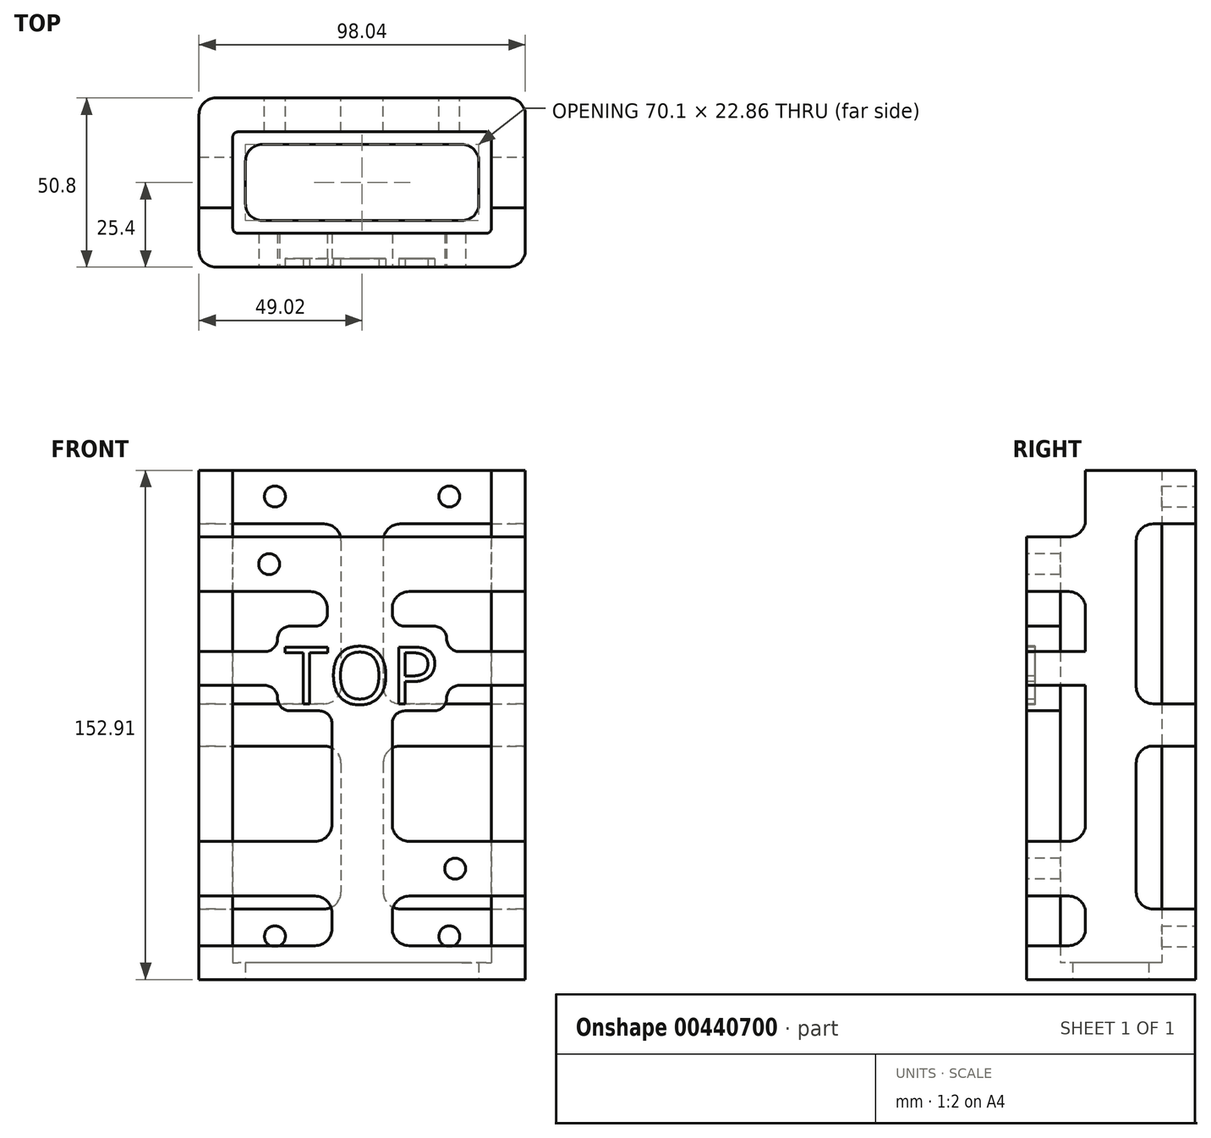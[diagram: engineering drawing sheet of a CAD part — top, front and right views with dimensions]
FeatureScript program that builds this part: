
annotation { "Feature Type Name" : "Feature", "Feature Type Description" : "" }
export const myFeature = defineFeature(function(context is Context, id is Id, definition is map)
    precondition{}
    {
        {
            var Q0;
            Q0=qCreatedBy(makeId("Top.planeOp"),FACE);
            var sketch = newSketch(context, id + "F0", { "sketchPlane" : qUnion([Q0])});
            skLineSegment(sketch, "E0.bottom", {"start": v(38.86, 15.24) * mm, "end": v(-38.86, 15.24) * mm});
            skLineSegment(sketch, "E0.top", {"start": v(38.86, -15.24) * mm, "end": v(-38.86, -15.24) * mm});
            skLineSegment(sketch, "E0.left", {"start": v(38.86, 15.24) * mm, "end": v(38.86, -15.24) * mm});
            skLineSegment(sketch, "E0.right", {"start": v(-38.86, 15.24) * mm, "end": v(-38.86, -15.24) * mm});
            skPoint(sketch, "E0.middle", {"position": v(0, 0) * mm});
            skLineSegment(sketch, "E1.bottom", {"start": v(49.02, -25.4) * mm, "end": v(-49.02, -25.4) * mm});
            skLineSegment(sketch, "E1.top", {"start": v(49.02, 25.4) * mm, "end": v(-49.02, 25.4) * mm});
            skLineSegment(sketch, "E1.left", {"start": v(49.02, -25.4) * mm, "end": v(49.02, 25.4) * mm});
            skLineSegment(sketch, "E1.right", {"start": v(-49.02, -25.4) * mm, "end": v(-49.02, 25.4) * mm});
            skSolve(sketch);
        }
        {
            var Q0;
            Q0 = qSketchRegion(id + "F0", true);
            extrude(context, id + "F1", {"entities" : qUnion([Q0]), "depth" : 152.9 * mm});
        }
        {
            var Q0;
            Q0=makeQuery(id+"F1.opExtrude","SWEPT_FACE",FACE,{"disambiguationData":[OSD([sQuery(id+"F0.wireOp",EDGE,"E1.bottom")])]});
            var sketch = newSketch(context, id + "F2", { "sketchPlane" : qUnion([Q0])});
            skCircle(sketch, "E2", {"center": v(-27.94, 124.71) * mm, "radius": 3.15 * mm});
            skCircle(sketch, "E3", {"center": v(27.94, 33.27) * mm, "radius": 3.15 * mm});
            skLineSegment(sketch, "E4", {"start": v(0, 0) * mm, "end": v(0, 152.9) * mm, "construction": true});
            skSolve(sketch);
        }
        {
            var Q0;
            Q0 = qSketchRegion(id + "F2", true);
            var Q1;
            Q1=makeQuery(id+"F1.opExtrude","SWEPT_FACE",FACE,{"disambiguationData":[OSD([sQuery(id+"F0.wireOp",EDGE,"E0.top")])]});
            extrude(context, id + "F3", {"entities" : qUnion([Q0]), "operationType" : NewBodyOperationType.REMOVE, "endBound" : BoundingType.UP_TO_SURFACE, "oppositeDirection" : true, "endBoundEntityFace" : qUnion([Q1]), "depth" : 25.4 * mm});
        }
        {
            var Q0;
            Q0=makeQuery(id+"F1.opExtrude","SWEPT_FACE",FACE,{"disambiguationData":[OSD([sQuery(id+"F0.wireOp",EDGE,"E1.bottom")])]});
            var sketch = newSketch(context, id + "F4", { "sketchPlane" : qUnion([Q0])});
            skText(sketch, "E5", { "text": "TOP", "fontName": "OpenSans-Regular.ttf"});
            skLineSegment(sketch, "E6", {"start": v(0, 152.9) * mm, "end": v(0, 0) * mm, "construction": true});
            const initialGuessF4  = {"E5": [-0.02337, 0.0827, 1, 0, 0.01728]};
            skSetInitialGuess(sketch, initialGuessF4);
            skSolve(sketch);
        }
        {
            var Q0;
            Q0 = qSketchRegion(id + "F4", true);
            extrude(context, id + "F5", {"entities" : qUnion([Q0]), "operationType" : NewBodyOperationType.REMOVE, "oppositeDirection" : true, "depth" : 2.54 * mm});
        }
        {
            var Q0;
            Q0=makeQuery(id+"F1.opExtrude","SWEPT_FACE",FACE,{"disambiguationData":[OSD([sQuery(id+"F0.wireOp",EDGE,"E1.top")])]});
            var sketch = newSketch(context, id + "F6", { "sketchPlane" : qUnion([Q0])});
            skCircle(sketch, "E7", {"center": v(26.2, 145.03) * mm, "radius": 3.15 * mm});
            skLineSegment(sketch, "E8", {"start": v(0, 0) * mm, "end": v(0, 152.9) * mm, "construction": true});
            skCircle(sketch, "E9.0.1.0", {"center": v(26.2, 12.95) * mm, "radius": 3.15 * mm});
            skCircle(sketch, "E9.1.0.0", {"center": v(-26.2, 145.03) * mm, "radius": 3.15 * mm});
            skCircle(sketch, "E9.1.1.0", {"center": v(-26.2, 12.95) * mm, "radius": 3.15 * mm});
            skLineSegment(sketch, "E9.direction1", {"start": v(26.2, 145.03) * mm, "end": v(-26.2, 145.03) * mm, "construction": true});
            skLineSegment(sketch, "E9.direction2", {"start": v(26.2, 145.03) * mm, "end": v(26.2, 12.95) * mm, "construction": true});
            skSolve(sketch);
        }
        {
            var Q0;
            Q0 = qSketchRegion(id + "F6", true);
            var Q1;
            Q1=makeQuery(id+"F1.opExtrude","SWEPT_FACE",FACE,{"disambiguationData":[OSD([sQuery(id+"F0.wireOp",EDGE,"E0.bottom")])]});
            extrude(context, id + "F7", {"entities" : qUnion([Q0]), "operationType" : NewBodyOperationType.REMOVE, "endBound" : BoundingType.UP_TO_SURFACE, "oppositeDirection" : true, "endBoundEntityFace" : qUnion([Q1]), "depth" : 25.4 * mm});
        }
        {
            var Q0;
            Q0=makeQuery(id+"F1.opExtrude","CAP_FACE",FACE,{"disambiguationData":[OSD([sQuery(id+"F0.wireOp",EDGE,"E0.bottom"),sQuery(id+"F0.wireOp",EDGE,"E0.top"),sQuery(id+"F0.wireOp",EDGE,"E0.left"),sQuery(id+"F0.wireOp",EDGE,"E0.right"),sQuery(id+"F0.wireOp",EDGE,"E1.bottom"),sQuery(id+"F0.wireOp",EDGE,"E1.top"),sQuery(id+"F0.wireOp",EDGE,"E1.left"),sQuery(id+"F0.wireOp",EDGE,"E1.right")])],"isStart":true});
            var sketch = newSketch(context, id + "F8", { "sketchPlane" : qUnion([Q0])});
            skLineSegment(sketch, "E10.bottom", {"start": v(38.86, 15.24) * mm, "end": v(-38.86, 15.24) * mm});
            skLineSegment(sketch, "E10.top", {"start": v(38.86, -15.24) * mm, "end": v(-38.86, -15.24) * mm});
            skLineSegment(sketch, "E10.left", {"start": v(38.86, 15.24) * mm, "end": v(38.86, -15.24) * mm});
            skLineSegment(sketch, "E10.right", {"start": v(-38.86, 15.24) * mm, "end": v(-38.86, -15.24) * mm});
            skPoint(sketch, "E10.middle", {"position": v(0, 0) * mm});
            skLineSegment(sketch, "E11.bottom", {"start": v(35.05, -11.43) * mm, "end": v(-35.05, -11.43) * mm});
            skLineSegment(sketch, "E11.top", {"start": v(35.05, 11.43) * mm, "end": v(-35.05, 11.43) * mm});
            skLineSegment(sketch, "E11.left", {"start": v(35.05, -11.43) * mm, "end": v(35.05, 11.43) * mm});
            skLineSegment(sketch, "E11.right", {"start": v(-35.05, -11.43) * mm, "end": v(-35.05, 11.43) * mm});
            skSolve(sketch);
        }
        {
            var Q0;
            Q0 = qSketchRegion(id + "F8", true);
            extrude(context, id + "F9", {"entities" : qUnion([Q0]), "operationType" : NewBodyOperationType.ADD, "oppositeDirection" : true, "depth" : 5.08 * mm});
        }
        {
            var Q0;
            Q0=makeQuery(id+"F1.opExtrude","SWEPT_EDGE",EDGE,{"disambiguationData":[OSD([sQuery(id+"F0.wireOp",EDGE,"E0.bottom"),sQuery(id+"F0.wireOp",EDGE,"E0.right")])]});
            var Q1;
            Q1=makeQuery(id+"F1.opExtrude","SWEPT_EDGE",EDGE,{"disambiguationData":[OSD([sQuery(id+"F0.wireOp",EDGE,"E0.top"),sQuery(id+"F0.wireOp",EDGE,"E0.right")])]});
            var Q2;
            Q2=makeQuery(id+"F1.opExtrude","SWEPT_EDGE",EDGE,{"disambiguationData":[OSD([sQuery(id+"F0.wireOp",EDGE,"E0.top"),sQuery(id+"F0.wireOp",EDGE,"E0.left")])]});
            var Q3;
            Q3=makeQuery(id+"F1.opExtrude","SWEPT_EDGE",EDGE,{"disambiguationData":[OSD([sQuery(id+"F0.wireOp",EDGE,"E0.bottom"),sQuery(id+"F0.wireOp",EDGE,"E0.left")])]});
            fillet(context, id + "F10", {"entities" : qUnion([Q0, Q1, Q2, Q3]), "radius" : 1.59 * mm, "tangentPropagation" : true, "allowEdgeOverflow" : false});
        }
        {
            var Q0;
            {var subQ1=sQuery(id+"F0.wireOp",EDGE,"E1.left");var subQ3=sQuery(id+"F0.wireOp",EDGE,"E1.bottom");Q0=makeQuery(id+"F5.boolean.opBoolean","SPLIT",FACE,{"disambiguationData":[TD([makeQuery(id+"F1.opExtrude","SWEPT_FACE",FACE,{"disambiguationData":[OSD([subQ1])]})])],"derivedFrom":makeQuery(id+"F1.opExtrude","SWEPT_FACE",FACE,{"disambiguationData":[OSD([subQ3])]})});}
            var sketch = newSketch(context, id + "F11", { "sketchPlane" : qUnion([Q0])});
            skLineSegment(sketch, "E12.bottom", {"start": v(49.02, 25.04) * mm, "end": v(9.05, 25.04) * mm});
            skLineSegment(sketch, "E12.top", {"start": v(49.02, 41.5) * mm, "end": v(9.05, 41.5) * mm});
            skLineSegment(sketch, "E13.left", {"start": v(9.05, 25.04) * mm, "end": v(9.05, 10.16) * mm});
            skLineSegment(sketch, "E13.right", {"start": v(-9.05, 25.04) * mm, "end": v(-9.05, 10.16) * mm});
            skLineSegment(sketch, "E14.trimOffspring", {"start": v(-9.05, 25.04) * mm, "end": v(-49.02, 25.04) * mm});
            skLineSegment(sketch, "E15", {"start": v(0, 0) * mm, "end": v(0, 152.9) * mm, "construction": true});
            skLineSegment(sketch, "E16.bottom", {"start": v(-49.02, 116.48) * mm, "end": v(-10.43, 116.48) * mm});
            skLineSegment(sketch, "E16.top", {"start": v(-49.02, 132.94) * mm, "end": v(9.05, 132.94) * mm});
            skLineSegment(sketch, "E17", {"start": v(49.02, 25.04) * mm, "end": v(49.02, 10.16) * mm});
            skLineSegment(sketch, "E18", {"start": v(49.02, 10.16) * mm, "end": v(9.05, 10.16) * mm});
            skLineSegment(sketch, "E19", {"start": v(-9.05, 10.16) * mm, "end": v(-49.02, 10.16) * mm});
            skLineSegment(sketch, "E20", {"start": v(-49.02, 10.16) * mm, "end": v(-49.02, 25.04) * mm});
            skLineSegment(sketch, "E21.left", {"start": v(9.05, 41.5) * mm, "end": v(9.05, 76.86) * mm});
            skLineSegment(sketch, "E21.right", {"start": v(-9.05, 41.5) * mm, "end": v(-9.05, 76.86) * mm});
            skLineSegment(sketch, "E22", {"start": v(49.02, 41.5) * mm, "end": v(49.02, 41.5) * mm});
            skLineSegment(sketch, "E23", {"start": v(9.05, 109.9) * mm, "end": v(9.05, 116.48) * mm});
            skLineSegment(sketch, "E24", {"start": v(-10.43, 109.9) * mm, "end": v(-10.43, 116.48) * mm});
            skLineSegment(sketch, "E25.trimOffspring", {"start": v(-9.05, 41.5) * mm, "end": v(-49.02, 41.5) * mm});
            skLineSegment(sketch, "E26.trimOffspring", {"start": v(9.05, 116.48) * mm, "end": v(49.02, 116.48) * mm});
            skLineSegment(sketch, "E27", {"start": v(-49.02, 98.46) * mm, "end": v(-49.02, 116.48) * mm});
            skLineSegment(sketch, "E28", {"start": v(49.02, 132.94) * mm, "end": v(49.02, 152.9) * mm});
            skLineSegment(sketch, "E29", {"start": v(49.02, 152.9) * mm, "end": v(-49.02, 152.9) * mm});
            skLineSegment(sketch, "E30", {"start": v(-49.02, 152.9) * mm, "end": v(-49.02, 132.94) * mm});
            skLineSegment(sketch, "E31.right", {"start": v(-49.02, 152.9) * mm, "end": v(-49.02, 152.9) * mm});
            skLineSegment(sketch, "E32.trimOffspring", {"start": v(9.05, 132.94) * mm, "end": v(49.02, 132.94) * mm});
            skLineSegment(sketch, "E33", {"start": v(9.05, 132.94) * mm, "end": v(9.05, 132.94) * mm});
            skPoint(sketch, "E34.visualSharp", {"position": v(-28.45, 89.67) * mm});
            skLineSegment(sketch, "E35", {"start": v(49.02, 116.48) * mm, "end": v(49.02, 98.48) * mm});
            skLineSegment(sketch, "E36", {"start": v(-49.02, 93.38) * mm, "end": v(49.02, 93.38) * mm, "construction": true});
            skLineSegment(sketch, "E37.bottom", {"start": v(-12.86, 80.67) * mm, "end": v(-21.59, 80.67) * mm});
            skLineSegment(sketch, "E37.top", {"start": v(21.59, 106.1) * mm, "end": v(12.86, 106.1) * mm});
            skLineSegment(sketch, "E37.left", {"start": v(25.4, 84.48) * mm, "end": v(25.4, 84.5) * mm});
            skLineSegment(sketch, "E37.right", {"start": v(-25.4, 84.48) * mm, "end": v(-25.4, 84.5) * mm});
            skPoint(sketch, "E37.middle", {"position": v(0, 93.38) * mm});
            skLineSegment(sketch, "E38.bottom", {"start": v(-49.02, 98.46) * mm, "end": v(-29.21, 98.46) * mm});
            skLineSegment(sketch, "E38.top", {"start": v(-49.02, 88.3) * mm, "end": v(-29.21, 88.3) * mm});
            skLineSegment(sketch, "E39.bottom", {"start": v(29.2, 98.48) * mm, "end": v(49.02, 98.48) * mm});
            skLineSegment(sketch, "E39.top", {"start": v(29.21, 88.3) * mm, "end": v(49.02, 88.3) * mm});
            skLineSegment(sketch, "E40.trimOffspring", {"start": v(-25.4, 102.27) * mm, "end": v(-25.4, 102.29) * mm});
            skLineSegment(sketch, "E41.trimOffspring", {"start": v(25.4, 102.29) * mm, "end": v(25.4, 102.29) * mm});
            skPoint(sketch, "E42.visualSharp", {"position": v(25.4, 106.1) * mm});
            skArc(sketch, "E42.filletArc", {"start": v(25.4, 102.29) * mm, "mid": v(24.28, 104.98) * mm, "end": v(21.59, 106.1) * mm});
            skPoint(sketch, "E43.visualSharp", {"position": v(25.4, 98.48) * mm});
            skArc(sketch, "E43.filletArc", {"start": v(25.4, 102.29) * mm, "mid": v(26.52, 99.6) * mm, "end": v(29.2, 98.48) * mm});
            skPoint(sketch, "E44.visualSharp", {"position": v(25.4, 88.3) * mm});
            skArc(sketch, "E44.filletArc", {"start": v(29.21, 88.3) * mm, "mid": v(26.52, 87.19) * mm, "end": v(25.4, 84.5) * mm});
            skPoint(sketch, "E45.visualSharp", {"position": v(25.4, 80.67) * mm});
            skArc(sketch, "E45.filletArc", {"start": v(21.59, 80.67) * mm, "mid": v(24.28, 81.79) * mm, "end": v(25.4, 84.48) * mm});
            skPoint(sketch, "E46.visualSharp", {"position": v(-25.4, 98.46) * mm});
            skArc(sketch, "E46.filletArc", {"start": v(-29.21, 98.46) * mm, "mid": v(-26.52, 99.58) * mm, "end": v(-25.4, 102.27) * mm});
            skPoint(sketch, "E47.visualSharp", {"position": v(-25.4, 106.1) * mm});
            skArc(sketch, "E47.filletArc", {"start": v(-21.6, 106.1) * mm, "mid": v(-24.28, 104.98) * mm, "end": v(-25.4, 102.29) * mm});
            skPoint(sketch, "E48.visualSharp", {"position": v(-25.4, 88.3) * mm});
            skArc(sketch, "E48.filletArc", {"start": v(-25.4, 84.5) * mm, "mid": v(-26.52, 87.19) * mm, "end": v(-29.21, 88.3) * mm});
            skPoint(sketch, "E49.visualSharp", {"position": v(-25.4, 80.67) * mm});
            skArc(sketch, "E49.filletArc", {"start": v(-25.4, 84.48) * mm, "mid": v(-24.28, 81.79) * mm, "end": v(-21.59, 80.67) * mm});
            skPoint(sketch, "E50.newPointA", {"position": v(-9.05, 80.67) * mm});
            skArc(sketch, "E50.filletArc", {"start": v(-9.05, 76.86) * mm, "mid": v(-10.16, 79.55) * mm, "end": v(-12.86, 80.67) * mm});
            skLineSegment(sketch, "E51", {"start": v(12.86, 80.67) * mm, "end": v(21.59, 80.67) * mm});
            skLineSegment(sketch, "E52.trimOffspring", {"start": v(-14.24, 106.1) * mm, "end": v(-21.6, 106.1) * mm});
            skPoint(sketch, "E53.visualSharp", {"position": v(9.05, 80.67) * mm});
            skArc(sketch, "E53.filletArc", {"start": v(12.86, 80.67) * mm, "mid": v(10.16, 79.55) * mm, "end": v(9.05, 76.86) * mm});
            skPoint(sketch, "E54.visualSharp", {"position": v(-10.43, 106.1) * mm});
            skArc(sketch, "E54.filletArc", {"start": v(-14.24, 106.1) * mm, "mid": v(-11.54, 107.21) * mm, "end": v(-10.43, 109.9) * mm});
            skPoint(sketch, "E55.visualSharp", {"position": v(9.05, 106.1) * mm});
            skArc(sketch, "E55.filletArc", {"start": v(9.05, 109.9) * mm, "mid": v(10.16, 107.21) * mm, "end": v(12.86, 106.1) * mm});
            skLineSegment(sketch, "E56", {"start": v(-49.02, 88.3) * mm, "end": v(-49.02, 41.5) * mm});
            skLineSegment(sketch, "E57", {"start": v(49.02, 88.3) * mm, "end": v(49.02, 41.5) * mm});
            skSolve(sketch);
        }
        {
            var Q0;
            Q0 = qSketchRegion(id + "F11", true);
            extrude(context, id + "F12", {"entities" : qUnion([Q0]), "operationType" : NewBodyOperationType.REMOVE, "oppositeDirection" : true, "depth" : 17.78 * mm});
        }
        {
            var Q0;
            Q0=makeQuery(id+"F1.opExtrude","SWEPT_FACE",FACE,{"disambiguationData":[OSD([sQuery(id+"F0.wireOp",EDGE,"E1.top")])]});
            var sketch = newSketch(context, id + "F13", { "sketchPlane" : qUnion([Q0])});
            skLineSegment(sketch, "E58.top", {"start": v(49.02, 21.18) * mm, "end": v(6.35, 21.18) * mm});
            skLineSegment(sketch, "E59.top", {"start": v(49.02, 136.8) * mm, "end": v(6.35, 136.8) * mm});
            skLineSegment(sketch, "E60", {"start": v(49.02, 76.45) * mm, "end": v(-49.02, 76.45) * mm, "construction": true});
            skLineSegment(sketch, "E61.bottom", {"start": v(49.02, 70.1) * mm, "end": v(6.35, 70.1) * mm});
            skLineSegment(sketch, "E61.top", {"start": v(49.02, 82.8) * mm, "end": v(6.35, 82.8) * mm});
            skLineSegment(sketch, "E62", {"start": v(0, 0) * mm, "end": v(0, 152.9) * mm, "construction": true});
            skLineSegment(sketch, "E63.left", {"start": v(6.35, 21.18) * mm, "end": v(6.35, 70.1) * mm});
            skLineSegment(sketch, "E63.right", {"start": v(-6.35, 21.18) * mm, "end": v(-6.35, 70.1) * mm});
            skLineSegment(sketch, "E64.trimOffspring", {"start": v(-6.35, 70.1) * mm, "end": v(-49.02, 70.1) * mm});
            skLineSegment(sketch, "E65.trimOffspring", {"start": v(-6.35, 82.8) * mm, "end": v(-49.02, 82.8) * mm});
            skLineSegment(sketch, "E66.trimOffspring", {"start": v(6.35, 82.8) * mm, "end": v(6.35, 136.8) * mm});
            skLineSegment(sketch, "E67.trimOffspring", {"start": v(-6.35, 82.8) * mm, "end": v(-6.35, 136.8) * mm});
            skLineSegment(sketch, "E68.trimOffspring", {"start": v(-6.35, 21.18) * mm, "end": v(-49.02, 21.18) * mm});
            skLineSegment(sketch, "E69.trimOffspring", {"start": v(-6.35, 136.8) * mm, "end": v(-49.02, 136.8) * mm});
            skLineSegment(sketch, "E70", {"start": v(49.02, 70.1) * mm, "end": v(49.02, 21.18) * mm});
            skLineSegment(sketch, "E71", {"start": v(49.02, 136.8) * mm, "end": v(49.02, 82.8) * mm});
            skLineSegment(sketch, "E72", {"start": v(-49.02, 136.8) * mm, "end": v(-49.02, 82.8) * mm});
            skLineSegment(sketch, "E73", {"start": v(-49.02, 70.1) * mm, "end": v(-49.02, 21.18) * mm});
            skSolve(sketch);
        }
        {
            var Q0;
            Q0 = qSketchRegion(id + "F13", true);
            extrude(context, id + "F14", {"entities" : qUnion([Q0]), "operationType" : NewBodyOperationType.REMOVE, "oppositeDirection" : true, "depth" : 17.78 * mm});
        }
        {
            var Q0;
            Q0=makeQuery(id+"F12.boolean.opBoolean","COPY",EDGE,{"derivedFrom":makeQuery(id+"F12.opExtrude","CAP_EDGE",EDGE,{"disambiguationData":[OSD([sQuery(id+"F11.wireOp",EDGE,"E18")])],"isStart":false})});
            var Q1;
            Q1=makeQuery(id+"F12.boolean.opBoolean","COPY",EDGE,{"derivedFrom":makeQuery(id+"F12.opExtrude","SWEPT_EDGE",EDGE,{"disambiguationData":[OSD([sQuery(id+"F11.wireOp",EDGE,"E13.left"),sQuery(id+"F11.wireOp",EDGE,"E18")])]})});
            var Q2;
            Q2=makeQuery(id+"F12.boolean.opBoolean","COPY",EDGE,{"derivedFrom":makeQuery(id+"F12.opExtrude","SWEPT_EDGE",EDGE,{"disambiguationData":[OSD([sQuery(id+"F11.wireOp",EDGE,"E12.bottom"),sQuery(id+"F11.wireOp",EDGE,"E13.left")])]})});
            var Q3;
            Q3=makeQuery(id+"F12.boolean.opBoolean","COPY",EDGE,{"derivedFrom":makeQuery(id+"F12.opExtrude","CAP_EDGE",EDGE,{"disambiguationData":[OSD([sQuery(id+"F11.wireOp",EDGE,"E12.bottom")])],"isStart":false})});
            var Q4;
            Q4=makeQuery(id+"F12.boolean.opBoolean","COPY",EDGE,{"derivedFrom":makeQuery(id+"F12.opExtrude","SWEPT_EDGE",EDGE,{"disambiguationData":[OSD([sQuery(id+"F11.wireOp",EDGE,"E13.right"),sQuery(id+"F11.wireOp",EDGE,"E19")])]})});
            var Q5;
            Q5=makeQuery(id+"F12.boolean.opBoolean","COPY",EDGE,{"derivedFrom":makeQuery(id+"F12.opExtrude","SWEPT_EDGE",EDGE,{"disambiguationData":[OSD([sQuery(id+"F11.wireOp",EDGE,"E13.right"),sQuery(id+"F11.wireOp",EDGE,"E14.trimOffspring")])]})});
            var Q6;
            Q6=makeQuery(id+"F12.boolean.opBoolean","COPY",EDGE,{"derivedFrom":makeQuery(id+"F12.opExtrude","CAP_EDGE",EDGE,{"disambiguationData":[OSD([sQuery(id+"F11.wireOp",EDGE,"E14.trimOffspring")])],"isStart":false})});
            var Q7;
            Q7=makeQuery(id+"F12.boolean.opBoolean","COPY",EDGE,{"derivedFrom":makeQuery(id+"F12.opExtrude","CAP_EDGE",EDGE,{"disambiguationData":[OSD([sQuery(id+"F11.wireOp",EDGE,"E19")])],"isStart":false})});
            var Q8;
            Q8=makeQuery(id+"F12.boolean.opBoolean","COPY",EDGE,{"derivedFrom":makeQuery(id+"F12.opExtrude","CAP_EDGE",EDGE,{"disambiguationData":[OSD([sQuery(id+"F11.wireOp",EDGE,"E25.trimOffspring")])],"isStart":false})});
            var Q9;
            Q9=makeQuery(id+"F12.boolean.opBoolean","COPY",EDGE,{"derivedFrom":makeQuery(id+"F12.opExtrude","SWEPT_EDGE",EDGE,{"disambiguationData":[OSD([sQuery(id+"F11.wireOp",EDGE,"E21.right"),sQuery(id+"F11.wireOp",EDGE,"E25.trimOffspring")])]})});
            var Q10;
            Q10=makeQuery(id+"F12.boolean.opBoolean","COPY",EDGE,{"derivedFrom":makeQuery(id+"F12.opExtrude","SWEPT_EDGE",EDGE,{"disambiguationData":[OSD([sQuery(id+"F11.wireOp",EDGE,"E21.right"),sQuery(id+"F11.wireOp",EDGE,"4d2d0d0c-2c55-4c6a-b625-4996a5f88d60.trimOffspring")])]})});
            var Q11;
            Q11=makeQuery(id+"F12.boolean.opBoolean","COPY",EDGE,{"derivedFrom":makeQuery(id+"F12.opExtrude","CAP_EDGE",EDGE,{"disambiguationData":[OSD([sQuery(id+"F11.wireOp",EDGE,"VWJKnyt0-ikCH-an2D-5rpM-SQd4CROjgRes")])],"isStart":false})});
            var Q12;
            Q12=makeQuery(id+"F12.boolean.opBoolean","COPY",EDGE,{"derivedFrom":makeQuery(id+"F12.opExtrude","CAP_EDGE",EDGE,{"disambiguationData":[OSD([sQuery(id+"F11.wireOp",EDGE,"E12.top")])],"isStart":false})});
            var Q13;
            Q13=makeQuery(id+"F12.boolean.opBoolean","COPY",EDGE,{"derivedFrom":makeQuery(id+"F12.opExtrude","SWEPT_EDGE",EDGE,{"disambiguationData":[OSD([sQuery(id+"F11.wireOp",EDGE,"E12.top"),sQuery(id+"F11.wireOp",EDGE,"E21.left")])]})});
            var Q14;
            Q14=makeQuery(id+"F12.boolean.opBoolean","COPY",EDGE,{"derivedFrom":makeQuery(id+"F12.opExtrude","SWEPT_EDGE",EDGE,{"disambiguationData":[OSD([sQuery(id+"F11.wireOp",EDGE,"XD9wa6Ai-1bgd-9dnm-z7rw-77nBXFs0ypjT.bottom"),sQuery(id+"F11.wireOp",EDGE,"E21.left")])]})});
            var Q15;
            Q15=makeQuery(id+"F12.boolean.opBoolean","COPY",EDGE,{"derivedFrom":makeQuery(id+"F12.opExtrude","CAP_EDGE",EDGE,{"disambiguationData":[OSD([sQuery(id+"F11.wireOp",EDGE,"JPwqmcXB-5S1r-1vy0-smpH-PhB2agzvwfZ4.bottom")])],"isStart":false})});
            var Q16;
            Q16=makeQuery(id+"F12.boolean.opBoolean","COPY",EDGE,{"derivedFrom":makeQuery(id+"F12.opExtrude","CAP_EDGE",EDGE,{"disambiguationData":[OSD([sQuery(id+"F11.wireOp",EDGE,"58QNkAeS-Yhub-D5n1-2TXT-XVsKPf8zmxOs")])],"isStart":false})});
            var Q17;
            Q17=makeQuery(id+"F12.boolean.opBoolean","COPY",EDGE,{"derivedFrom":makeQuery(id+"F12.opExtrude","CAP_EDGE",EDGE,{"disambiguationData":[OSD([sQuery(id+"F11.wireOp",EDGE,"E16.bottom")])],"isStart":false})});
            var Q18;
            Q18=makeQuery(id+"F12.boolean.opBoolean","COPY",EDGE,{"derivedFrom":makeQuery(id+"F12.opExtrude","SWEPT_EDGE",EDGE,{"disambiguationData":[OSD([sQuery(id+"F11.wireOp",EDGE,"E24"),sQuery(id+"F11.wireOp",EDGE,"8e6880b3-bb9e-4e0c-a185-ce6dc9b62ba0.trimOffspring")])]})});
            var Q19;
            Q19=makeQuery(id+"F12.boolean.opBoolean","COPY",EDGE,{"derivedFrom":makeQuery(id+"F12.opExtrude","SWEPT_EDGE",EDGE,{"disambiguationData":[OSD([sQuery(id+"F11.wireOp",EDGE,"E16.bottom"),sQuery(id+"F11.wireOp",EDGE,"E24")])]})});
            var Q20;
            Q20=makeQuery(id+"F12.boolean.opBoolean","COPY",EDGE,{"derivedFrom":makeQuery(id+"F12.opExtrude","SWEPT_EDGE",EDGE,{"disambiguationData":[OSD([sQuery(id+"F11.wireOp",EDGE,"XD9wa6Ai-1bgd-9dnm-z7rw-77nBXFs0ypjT.top"),sQuery(id+"F11.wireOp",EDGE,"E23")])]})});
            var Q21;
            Q21=makeQuery(id+"F12.boolean.opBoolean","COPY",EDGE,{"derivedFrom":makeQuery(id+"F12.opExtrude","SWEPT_EDGE",EDGE,{"disambiguationData":[OSD([sQuery(id+"F11.wireOp",EDGE,"E23"),sQuery(id+"F11.wireOp",EDGE,"E26.trimOffspring")])]})});
            var Q22;
            Q22=makeQuery(id+"F12.boolean.opBoolean","COPY",EDGE,{"derivedFrom":makeQuery(id+"F12.opExtrude","CAP_EDGE",EDGE,{"disambiguationData":[OSD([sQuery(id+"F11.wireOp",EDGE,"JPwqmcXB-5S1r-1vy0-smpH-PhB2agzvwfZ4.top")])],"isStart":false})});
            var Q23;
            Q23=makeQuery(id+"F12.boolean.opBoolean","COPY",EDGE,{"derivedFrom":makeQuery(id+"F12.opExtrude","CAP_EDGE",EDGE,{"disambiguationData":[OSD([sQuery(id+"F11.wireOp",EDGE,"E26.trimOffspring")])],"isStart":false})});
            var Q24;
            {var subQ0=sQuery(id+"F11.wireOp",EDGE,"E33");var subQ1=sQuery(id+"F11.wireOp",EDGE,"E32.trimOffspring");var subQ2=sQuery(id+"F11.wireOp",EDGE,"E16.top");Q24=makeQuery(id+"F12.boolean.opBoolean","COPY",EDGE,{"disambiguationData":[TD([makeQuery(id+"F1.opExtrude","SWEPT_FACE",FACE,{"disambiguationData":[OSD([sQuery(id+"F0.wireOp",EDGE,"E0.left")])]})])],"derivedFrom":makeQuery(id+"F12.opExtrude","CAP_EDGE",EDGE,{"disambiguationData":[OSD([subQ2,subQ1,subQ0])],"isStart":false})});}
            var Q25;
            {var subQ0=sQuery(id+"F11.wireOp",EDGE,"E33");var subQ1=sQuery(id+"F11.wireOp",EDGE,"E32.trimOffspring");var subQ2=sQuery(id+"F11.wireOp",EDGE,"E16.top");Q25=makeQuery(id+"F12.boolean.opBoolean","COPY",EDGE,{"disambiguationData":[TD([makeQuery(id+"F1.opExtrude","SWEPT_FACE",FACE,{"disambiguationData":[OSD([sQuery(id+"F0.wireOp",EDGE,"E0.right")])]})])],"derivedFrom":makeQuery(id+"F12.opExtrude","CAP_EDGE",EDGE,{"disambiguationData":[OSD([subQ2,subQ1,subQ0])],"isStart":false})});}
            var Q26;
            Q26=makeQuery(id+"F14.boolean.opBoolean","COPY",EDGE,{"derivedFrom":makeQuery(id+"F14.opExtrude","CAP_EDGE",EDGE,{"disambiguationData":[OSD([sQuery(id+"F13.wireOp",EDGE,"E61.bottom")])],"isStart":false})});
            var Q27;
            Q27=makeQuery(id+"F14.boolean.opBoolean","COPY",EDGE,{"derivedFrom":makeQuery(id+"F14.opExtrude","CAP_EDGE",EDGE,{"disambiguationData":[OSD([sQuery(id+"F13.wireOp",EDGE,"E61.top")])],"isStart":false})});
            var Q28;
            Q28=makeQuery(id+"F14.boolean.opBoolean","COPY",EDGE,{"derivedFrom":makeQuery(id+"F14.opExtrude","CAP_EDGE",EDGE,{"disambiguationData":[OSD([sQuery(id+"F13.wireOp",EDGE,"E58.top")])],"isStart":false})});
            var Q29;
            Q29=makeQuery(id+"F14.boolean.opBoolean","COPY",EDGE,{"derivedFrom":makeQuery(id+"F14.opExtrude","SWEPT_EDGE",EDGE,{"disambiguationData":[OSD([sQuery(id+"F13.wireOp",EDGE,"E58.top"),sQuery(id+"F13.wireOp",EDGE,"E63.left")])]})});
            var Q30;
            Q30=makeQuery(id+"F14.boolean.opBoolean","COPY",EDGE,{"derivedFrom":makeQuery(id+"F14.opExtrude","SWEPT_EDGE",EDGE,{"disambiguationData":[OSD([sQuery(id+"F13.wireOp",EDGE,"E61.bottom"),sQuery(id+"F13.wireOp",EDGE,"E63.left")])]})});
            var Q31;
            Q31=makeQuery(id+"F14.boolean.opBoolean","COPY",EDGE,{"derivedFrom":makeQuery(id+"F14.opExtrude","SWEPT_EDGE",EDGE,{"disambiguationData":[OSD([sQuery(id+"F13.wireOp",EDGE,"E61.top"),sQuery(id+"F13.wireOp",EDGE,"E66.trimOffspring")])]})});
            var Q32;
            Q32=makeQuery(id+"F14.boolean.opBoolean","COPY",EDGE,{"derivedFrom":makeQuery(id+"F14.opExtrude","CAP_EDGE",EDGE,{"disambiguationData":[OSD([sQuery(id+"F13.wireOp",EDGE,"E59.top")])],"isStart":false})});
            var Q33;
            Q33=makeQuery(id+"F14.boolean.opBoolean","COPY",EDGE,{"derivedFrom":makeQuery(id+"F14.opExtrude","SWEPT_EDGE",EDGE,{"disambiguationData":[OSD([sQuery(id+"F13.wireOp",EDGE,"E59.top"),sQuery(id+"F13.wireOp",EDGE,"E66.trimOffspring")])]})});
            var Q34;
            Q34=makeQuery(id+"F14.boolean.opBoolean","COPY",EDGE,{"derivedFrom":makeQuery(id+"F14.opExtrude","SWEPT_EDGE",EDGE,{"disambiguationData":[OSD([sQuery(id+"F13.wireOp",EDGE,"E67.trimOffspring"),sQuery(id+"F13.wireOp",EDGE,"E69.trimOffspring")])]})});
            var Q35;
            Q35=makeQuery(id+"F14.boolean.opBoolean","COPY",EDGE,{"derivedFrom":makeQuery(id+"F14.opExtrude","CAP_EDGE",EDGE,{"disambiguationData":[OSD([sQuery(id+"F13.wireOp",EDGE,"E69.trimOffspring")])],"isStart":false})});
            var Q36;
            Q36=makeQuery(id+"F14.boolean.opBoolean","COPY",EDGE,{"derivedFrom":makeQuery(id+"F14.opExtrude","SWEPT_EDGE",EDGE,{"disambiguationData":[OSD([sQuery(id+"F13.wireOp",EDGE,"E65.trimOffspring"),sQuery(id+"F13.wireOp",EDGE,"E67.trimOffspring")])]})});
            var Q37;
            Q37=makeQuery(id+"F14.boolean.opBoolean","COPY",EDGE,{"derivedFrom":makeQuery(id+"F14.opExtrude","CAP_EDGE",EDGE,{"disambiguationData":[OSD([sQuery(id+"F13.wireOp",EDGE,"E65.trimOffspring")])],"isStart":false})});
            var Q38;
            Q38=makeQuery(id+"F14.boolean.opBoolean","COPY",EDGE,{"derivedFrom":makeQuery(id+"F14.opExtrude","SWEPT_EDGE",EDGE,{"disambiguationData":[OSD([sQuery(id+"F13.wireOp",EDGE,"E63.right"),sQuery(id+"F13.wireOp",EDGE,"E68.trimOffspring")])]})});
            var Q39;
            Q39=makeQuery(id+"F14.boolean.opBoolean","COPY",EDGE,{"derivedFrom":makeQuery(id+"F14.opExtrude","SWEPT_EDGE",EDGE,{"disambiguationData":[OSD([sQuery(id+"F13.wireOp",EDGE,"E63.right"),sQuery(id+"F13.wireOp",EDGE,"E64.trimOffspring")])]})});
            var Q40;
            Q40=makeQuery(id+"F14.boolean.opBoolean","COPY",EDGE,{"derivedFrom":makeQuery(id+"F14.opExtrude","CAP_EDGE",EDGE,{"disambiguationData":[OSD([sQuery(id+"F13.wireOp",EDGE,"E64.trimOffspring")])],"isStart":false})});
            var Q41;
            Q41=makeQuery(id+"F14.boolean.opBoolean","COPY",EDGE,{"derivedFrom":makeQuery(id+"F14.opExtrude","CAP_EDGE",EDGE,{"disambiguationData":[OSD([sQuery(id+"F13.wireOp",EDGE,"E68.trimOffspring")])],"isStart":false})});
            var Q42;
            {var subQ0=sQuery(id+"F0.wireOp",EDGE,"E1.bottom");var subQ1=sQuery(id+"F0.wireOp",EDGE,"E1.left");Q42=makeQuery(id+"F12.boolean.opBoolean","SPLIT",EDGE,{"disambiguationData":[TD([makeQuery(id+"F12.opExtrude","SWEPT_FACE",FACE,{"disambiguationData":[OSD([sQuery(id+"F11.wireOp",EDGE,"E26.trimOffspring")])]})])],"derivedFrom":makeQuery(id+"F1.opExtrude","SWEPT_EDGE",EDGE,{"disambiguationData":[OSD([subQ0,subQ1])]})});}
            var Q43;
            {var subQ0=sQuery(id+"F0.wireOp",EDGE,"E1.bottom");var subQ1=sQuery(id+"F0.wireOp",EDGE,"E1.left");Q43=makeQuery(id+"F12.boolean.opBoolean","SPLIT",EDGE,{"disambiguationData":[TD([makeQuery(id+"F12.opExtrude","SWEPT_FACE",FACE,{"disambiguationData":[OSD([sQuery(id+"F11.wireOp",EDGE,"JPwqmcXB-5S1r-1vy0-smpH-PhB2agzvwfZ4.bottom")])]})])],"derivedFrom":makeQuery(id+"F1.opExtrude","SWEPT_EDGE",EDGE,{"disambiguationData":[OSD([subQ0,subQ1])]})});}
            var Q44;
            {var subQ0=sQuery(id+"F0.wireOp",EDGE,"E1.bottom");var subQ1=sQuery(id+"F0.wireOp",EDGE,"E1.left");Q44=makeQuery(id+"F12.boolean.opBoolean","SPLIT",EDGE,{"disambiguationData":[TD([makeQuery(id+"F12.opExtrude","SWEPT_FACE",FACE,{"disambiguationData":[OSD([sQuery(id+"F11.wireOp",EDGE,"E12.bottom")])]})])],"derivedFrom":makeQuery(id+"F1.opExtrude","SWEPT_EDGE",EDGE,{"disambiguationData":[OSD([subQ0,subQ1])]})});}
            var Q45;
            {var subQ0=sQuery(id+"F0.wireOp",EDGE,"E1.left");var subQ1=sQuery(id+"F0.wireOp",EDGE,"E1.bottom");Q45=makeQuery(id+"F12.boolean.opBoolean","SPLIT",EDGE,{"disambiguationData":[TD([makeQuery(id+"F12.opExtrude","SWEPT_FACE",FACE,{"disambiguationData":[OSD([sQuery(id+"F11.wireOp",EDGE,"E18")])]})])],"derivedFrom":makeQuery(id+"F1.opExtrude","SWEPT_EDGE",EDGE,{"disambiguationData":[OSD([subQ1,subQ0])]})});}
            var Q46;
            {var subQ0=sQuery(id+"F0.wireOp",EDGE,"E1.left");var subQ1=sQuery(id+"F0.wireOp",EDGE,"E1.top");Q46=makeQuery(id+"F14.boolean.opBoolean","SPLIT",EDGE,{"disambiguationData":[TD([makeQuery(id+"F14.opExtrude","SWEPT_FACE",FACE,{"disambiguationData":[OSD([sQuery(id+"F13.wireOp",EDGE,"E68.trimOffspring")])]})])],"derivedFrom":makeQuery(id+"F1.opExtrude","SWEPT_EDGE",EDGE,{"disambiguationData":[OSD([subQ1,subQ0])]})});}
            var Q47;
            {var subQ0=sQuery(id+"F0.wireOp",EDGE,"E1.top");var subQ1=sQuery(id+"F0.wireOp",EDGE,"E1.left");Q47=makeQuery(id+"F14.boolean.opBoolean","SPLIT",EDGE,{"disambiguationData":[TD([makeQuery(id+"F14.opExtrude","SWEPT_FACE",FACE,{"disambiguationData":[OSD([sQuery(id+"F13.wireOp",EDGE,"E64.trimOffspring")])]})])],"derivedFrom":makeQuery(id+"F1.opExtrude","SWEPT_EDGE",EDGE,{"disambiguationData":[OSD([subQ0,subQ1])]})});}
            var Q48;
            {var subQ0=sQuery(id+"F0.wireOp",EDGE,"E1.left");var subQ1=sQuery(id+"F0.wireOp",EDGE,"E1.top");Q48=makeQuery(id+"F14.boolean.opBoolean","SPLIT",EDGE,{"disambiguationData":[TD([makeQuery(id+"F14.opExtrude","SWEPT_FACE",FACE,{"disambiguationData":[OSD([sQuery(id+"F13.wireOp",EDGE,"E69.trimOffspring")])]})])],"derivedFrom":makeQuery(id+"F1.opExtrude","SWEPT_EDGE",EDGE,{"disambiguationData":[OSD([subQ1,subQ0])]})});}
            var Q49;
            {var subQ0=sQuery(id+"F0.wireOp",EDGE,"E1.right");var subQ1=sQuery(id+"F0.wireOp",EDGE,"E1.top");Q49=makeQuery(id+"F14.boolean.opBoolean","SPLIT",EDGE,{"disambiguationData":[TD([makeQuery(id+"F14.opExtrude","SWEPT_FACE",FACE,{"disambiguationData":[OSD([sQuery(id+"F13.wireOp",EDGE,"E59.top")])]})])],"derivedFrom":makeQuery(id+"F1.opExtrude","SWEPT_EDGE",EDGE,{"disambiguationData":[OSD([subQ1,subQ0])]})});}
            var Q50;
            {var subQ0=sQuery(id+"F0.wireOp",EDGE,"E1.top");var subQ1=sQuery(id+"F0.wireOp",EDGE,"E1.right");Q50=makeQuery(id+"F14.boolean.opBoolean","SPLIT",EDGE,{"disambiguationData":[TD([makeQuery(id+"F14.opExtrude","SWEPT_FACE",FACE,{"disambiguationData":[OSD([sQuery(id+"F13.wireOp",EDGE,"E61.bottom")])]})])],"derivedFrom":makeQuery(id+"F1.opExtrude","SWEPT_EDGE",EDGE,{"disambiguationData":[OSD([subQ0,subQ1])]})});}
            var Q51;
            {var subQ0=sQuery(id+"F0.wireOp",EDGE,"E1.right");var subQ1=sQuery(id+"F0.wireOp",EDGE,"E1.top");Q51=makeQuery(id+"F14.boolean.opBoolean","SPLIT",EDGE,{"disambiguationData":[TD([makeQuery(id+"F14.opExtrude","SWEPT_FACE",FACE,{"disambiguationData":[OSD([sQuery(id+"F13.wireOp",EDGE,"E58.top")])]})])],"derivedFrom":makeQuery(id+"F1.opExtrude","SWEPT_EDGE",EDGE,{"disambiguationData":[OSD([subQ1,subQ0])]})});}
            var Q52;
            {var subQ0=sQuery(id+"F0.wireOp",EDGE,"E1.right");var subQ1=sQuery(id+"F0.wireOp",EDGE,"E1.bottom");Q52=makeQuery(id+"F12.boolean.opBoolean","SPLIT",EDGE,{"disambiguationData":[TD([makeQuery(id+"F12.opExtrude","SWEPT_FACE",FACE,{"disambiguationData":[OSD([sQuery(id+"F11.wireOp",EDGE,"E19")])]})])],"derivedFrom":makeQuery(id+"F1.opExtrude","SWEPT_EDGE",EDGE,{"disambiguationData":[OSD([subQ1,subQ0])]})});}
            var Q53;
            {var subQ0=sQuery(id+"F0.wireOp",EDGE,"E1.bottom");var subQ1=sQuery(id+"F0.wireOp",EDGE,"E1.right");Q53=makeQuery(id+"F12.boolean.opBoolean","SPLIT",EDGE,{"disambiguationData":[TD([makeQuery(id+"F12.opExtrude","SWEPT_FACE",FACE,{"disambiguationData":[OSD([sQuery(id+"F11.wireOp",EDGE,"E14.trimOffspring")])]})])],"derivedFrom":makeQuery(id+"F1.opExtrude","SWEPT_EDGE",EDGE,{"disambiguationData":[OSD([subQ0,subQ1])]})});}
            var Q54;
            {var subQ0=sQuery(id+"F0.wireOp",EDGE,"E1.bottom");var subQ1=sQuery(id+"F0.wireOp",EDGE,"E1.right");Q54=makeQuery(id+"F12.boolean.opBoolean","SPLIT",EDGE,{"disambiguationData":[TD([makeQuery(id+"F12.opExtrude","SWEPT_FACE",FACE,{"disambiguationData":[OSD([sQuery(id+"F11.wireOp",EDGE,"VWJKnyt0-ikCH-an2D-5rpM-SQd4CROjgRes")])]})])],"derivedFrom":makeQuery(id+"F1.opExtrude","SWEPT_EDGE",EDGE,{"disambiguationData":[OSD([subQ0,subQ1])]})});}
            var Q55;
            {var subQ0=sQuery(id+"F0.wireOp",EDGE,"E1.bottom");var subQ1=sQuery(id+"F0.wireOp",EDGE,"E1.right");Q55=makeQuery(id+"F12.boolean.opBoolean","SPLIT",EDGE,{"disambiguationData":[TD([makeQuery(id+"F12.opExtrude","SWEPT_FACE",FACE,{"disambiguationData":[OSD([sQuery(id+"F11.wireOp",EDGE,"E16.bottom")])]})])],"derivedFrom":makeQuery(id+"F1.opExtrude","SWEPT_EDGE",EDGE,{"disambiguationData":[OSD([subQ0,subQ1])]})});}
            var Q56;
            Q56=makeQuery(id+"F9.opExtrude","SWEPT_EDGE",EDGE,{"disambiguationData":[OSD([sQuery(id+"F8.wireOp",EDGE,"E11.top"),sQuery(id+"F8.wireOp",EDGE,"E11.left")])]});
            var Q57;
            Q57=makeQuery(id+"F9.opExtrude","SWEPT_EDGE",EDGE,{"disambiguationData":[OSD([sQuery(id+"F8.wireOp",EDGE,"E11.bottom"),sQuery(id+"F8.wireOp",EDGE,"E11.left")])]});
            var Q58;
            Q58=makeQuery(id+"F9.opExtrude","SWEPT_EDGE",EDGE,{"disambiguationData":[OSD([sQuery(id+"F8.wireOp",EDGE,"E11.top"),sQuery(id+"F8.wireOp",EDGE,"E11.right")])]});
            var Q59;
            Q59=makeQuery(id+"F9.opExtrude","SWEPT_EDGE",EDGE,{"disambiguationData":[OSD([sQuery(id+"F8.wireOp",EDGE,"E11.bottom"),sQuery(id+"F8.wireOp",EDGE,"E11.right")])]});
            var Q60;
            {var subQ0=sQuery(id+"F0.wireOp",EDGE,"E1.bottom");var subQ1=sQuery(id+"F0.wireOp",EDGE,"E1.left");Q60=makeQuery(id+"F12.boolean.opBoolean","SPLIT",EDGE,{"disambiguationData":[TD([makeQuery(id+"F12.opExtrude","SWEPT_FACE",FACE,{"disambiguationData":[OSD([sQuery(id+"F11.wireOp",EDGE,"E39.bottom")])]})])],"derivedFrom":makeQuery(id+"F1.opExtrude","SWEPT_EDGE",EDGE,{"disambiguationData":[OSD([subQ0,subQ1])]})});}
            var Q61;
            {var subQ0=sQuery(id+"F0.wireOp",EDGE,"E1.bottom");var subQ1=sQuery(id+"F0.wireOp",EDGE,"E1.right");Q61=makeQuery(id+"F12.boolean.opBoolean","SPLIT",EDGE,{"disambiguationData":[TD([makeQuery(id+"F12.opExtrude","SWEPT_FACE",FACE,{"disambiguationData":[OSD([sQuery(id+"F11.wireOp",EDGE,"E38.bottom")])]})])],"derivedFrom":makeQuery(id+"F1.opExtrude","SWEPT_EDGE",EDGE,{"disambiguationData":[OSD([subQ0,subQ1])]})});}
            fillet(context, id + "F15", {"entities" : qUnion([Q0, Q1, Q2, Q3, Q4, Q5, Q6, Q7, Q8, Q9, Q10, Q11, Q12, Q13, Q14, Q15, Q16, Q17, Q18, Q19, Q20, Q21, Q22, Q23, Q24, Q25, Q26, Q27, Q28, Q29, Q30, Q31, Q32, Q33, Q34, Q35, Q36, Q37, Q38, Q39, Q40, Q41, Q42, Q43, Q44, Q45, Q46, Q47, Q48, Q49, Q50, Q51, Q52, Q53, Q54, Q55, Q56, Q57, Q58, Q59, Q60, Q61]), "radius" : 5.08 * mm, "tangentPropagation" : true, "allowEdgeOverflow" : false});
        }
    });
